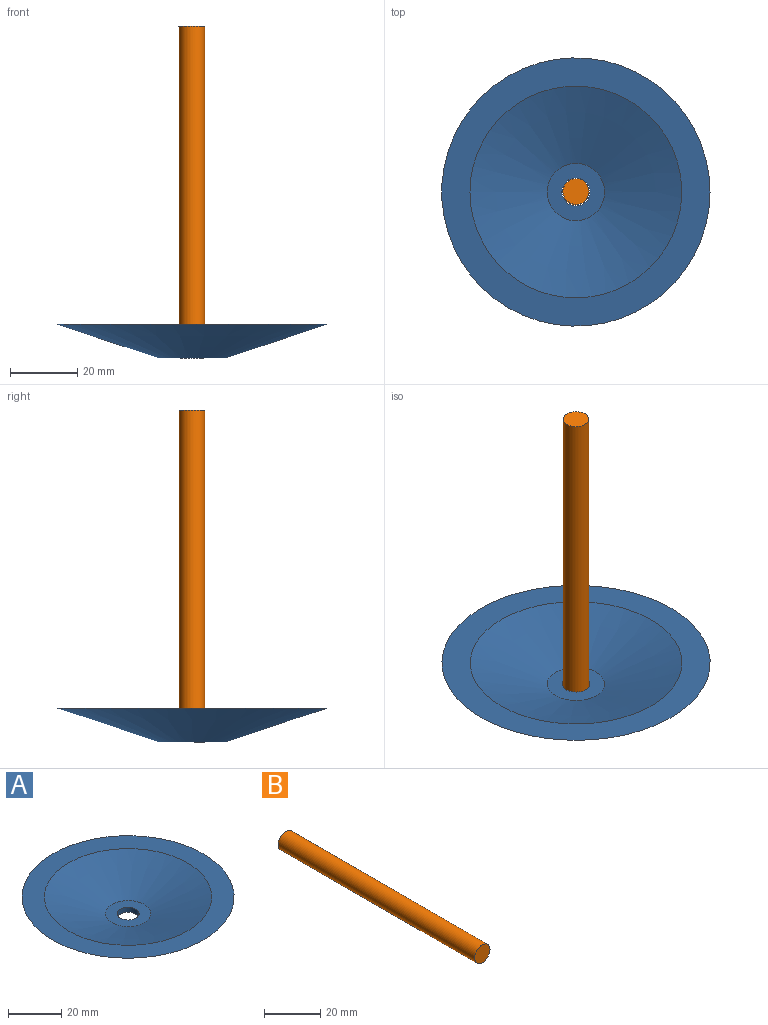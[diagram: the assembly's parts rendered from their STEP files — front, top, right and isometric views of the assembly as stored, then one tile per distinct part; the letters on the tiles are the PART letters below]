
ASSEMBLY  parts=2 mates=1
PART A: 6 faces, bbox 80x80x10 mm
  f0: plane 80x80mm, normal (0,0,1), area 1894.2mm2, adj f1,f3
  f1: cone r=10mm half-angle=71.6deg, axis (0,0,1), area 4967.3mm2, adj f0,f2
  f2: plane 20x20mm, normal (0,0,-1), area 260.1mm2, adj f1,f5
  f3: cone r=8.54mm half-angle=71.5deg, axis (0,0,1), area 3061.7mm2, adj f0,f4
  f4: plane 17.08x17.08mm, normal (0,0,1), area 175.1mm2, adj f3,f5
  f5: cylinder r=4.15mm len=8.3mm, axis (0,0,1), area 59.5mm2, adj f2,f4
PART B: 3 faces, bbox 7.7x99x7.7 mm
  f0: cylinder r=3.85mm len=99mm, axis (0,1,0), area 2394.8mm2, adj f1,f2
  f1: plane 7.7x7.7mm, normal (0,-1,0), area 46.6mm2, adj f0
  f2: plane 7.7x7.7mm, normal (0,1,0), area 46.6mm2, adj f0
PLACE A t=(-44.25,13.99,-14.95)mm
PLACE B rot(axis=(0.58,-0.58,-0.58),120deg) t=(-44.25,13.99,108.9)mm
MATE fastened B.f0 <-> A.f1  axis (0,0,-1) through (-44.25,13.99,9.9)mm
